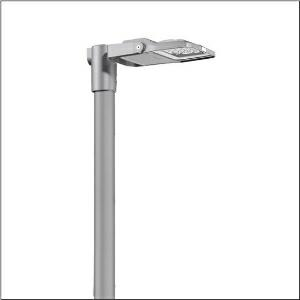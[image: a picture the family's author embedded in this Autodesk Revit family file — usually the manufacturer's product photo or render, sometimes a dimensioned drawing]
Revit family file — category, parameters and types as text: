
# Revit family: floodlight_fl_21_iq_micro___pl64_5xa7761a2e3a_b98d
name_source: partatom
category: Lighting Fixtures
units: mm (PartAtom-declared; Revit-internal decimal feet)

## family parameters
Cut with Voids When Loaded = No
Host = Face
Light Source = No
Part Type = Normal
Room Calculation Point = No
Round Connector Dimension = Use Diameter
Shared = No

## types (1)
- --- (1 x LED, 2870 lm, 23.1 W, 3000K)
    Apparent Load = 23 VA
    CIE Flux Codes = 28 80 98 100 100
    Color Rendering = 70
    Color Temperature = 3000K
    Default Elevation = 1800 mm
    Description = Floodlight FL 21 iQ micro, floodlight, primary light control with lens, of PMMA, primary optical cover: protective disc, of toughened safety glass, transparent, light distribution: PL64, light emission: direct distribution, installation type: surface-mounted, LED, High Power LED, rated luminous flux: 2.870lm, luminous efficacy: 124lm/W, light colour: 730, colour temperature: 3000K, control gear: iQ Comfort/DALI, control: optimised constant luminous flux control (CLO 2.0), Desk-Remote (wireless, voltage-free reading and setting of iQ features in the workshop via application-optimized NFC function/RFID function), Light-Fading, Smart-Wire, Night-Set, Lumen-Switch, Temp-Guard, Auto-Match, with terminal, 6-pole, mains connection: 220..240V, AC, 50/60Hz, start of lifetime: 23W, end of service life: 24W, reduction: 11W, luminaire housing, of diecast aluminium, powder-coated, Siteco® metallic grey (DB 702S), corrosivity category C5 mid according to DIN EN ISO 12944, suitable for swimming pools, chlorine-resistant, sealing non-destructively replaceable, please order mast flange separately, mast bracket, of steel, galvanised, powder-coated, Siteco® metallic grey (DB 702S), protection rating (complete): IP66, insulation class (complete): insulation class II (safety insulation), certification: CE, ENEC, VDE, protection symbol: D, impact resistance: IK07, permissible operating ambient temperature: -40..+40°C, permissible operating ambient temperature for outdoor applications: -40..+50°C, standard: DIN EN 12944, LABS conformity tested according to VDMA 24364:2018-05, packaging unit: 1 piece

Light Distribution: PL64
    Height = 65 mm
    Lamp = 1 x LED
    Lamp Light Flux = 2870 lm
    Lamp Power = 23.1 W
    Lamp count = 1
    Length = 312 mm
    Luminous efficacy = 124 lm/W
    Manufacturer = Siteco
    ModVariant = No
    Model = 5XA7761A2E3A
    Number of Poles = 1
    OnlyDefault = Yes
    Power Factor = 1
    Product Name = Floodlight FL 21 iQ micro | PL64
    Product group = floodlight | pylon top
    ProductGroupID = 6101
    Protection Class = Protection class II
    Protection Degree = IP 66
    RLX_Detail_Level = 1
    RLX_Emergency_Light_Flux = 0 lm
    RLX_Emergency_Type = 0
    RLX_Emergency_Type_DB = No
    RlxData = <blob elided: 101793 chars, md5=6414a949>
    Socket = socket
    Standby Power = 0 W
    System Light Flux = 2870 lm
    System Power = 23 W
    Type Comments = factory setting: luminous flux: 100 % | dim-lin: 254 | 455 mA
    Type Image = l_1007121.jpg
    URL = http://relux.com
    VarID = @adj_202257
    Voltage = 0 V
    Weight = 0.00 kg
    Width = 230 mm

## geometry (parser evidence)
native form markers: Blend x4, Sweep x11
no freeform markers — native parametric forms only
